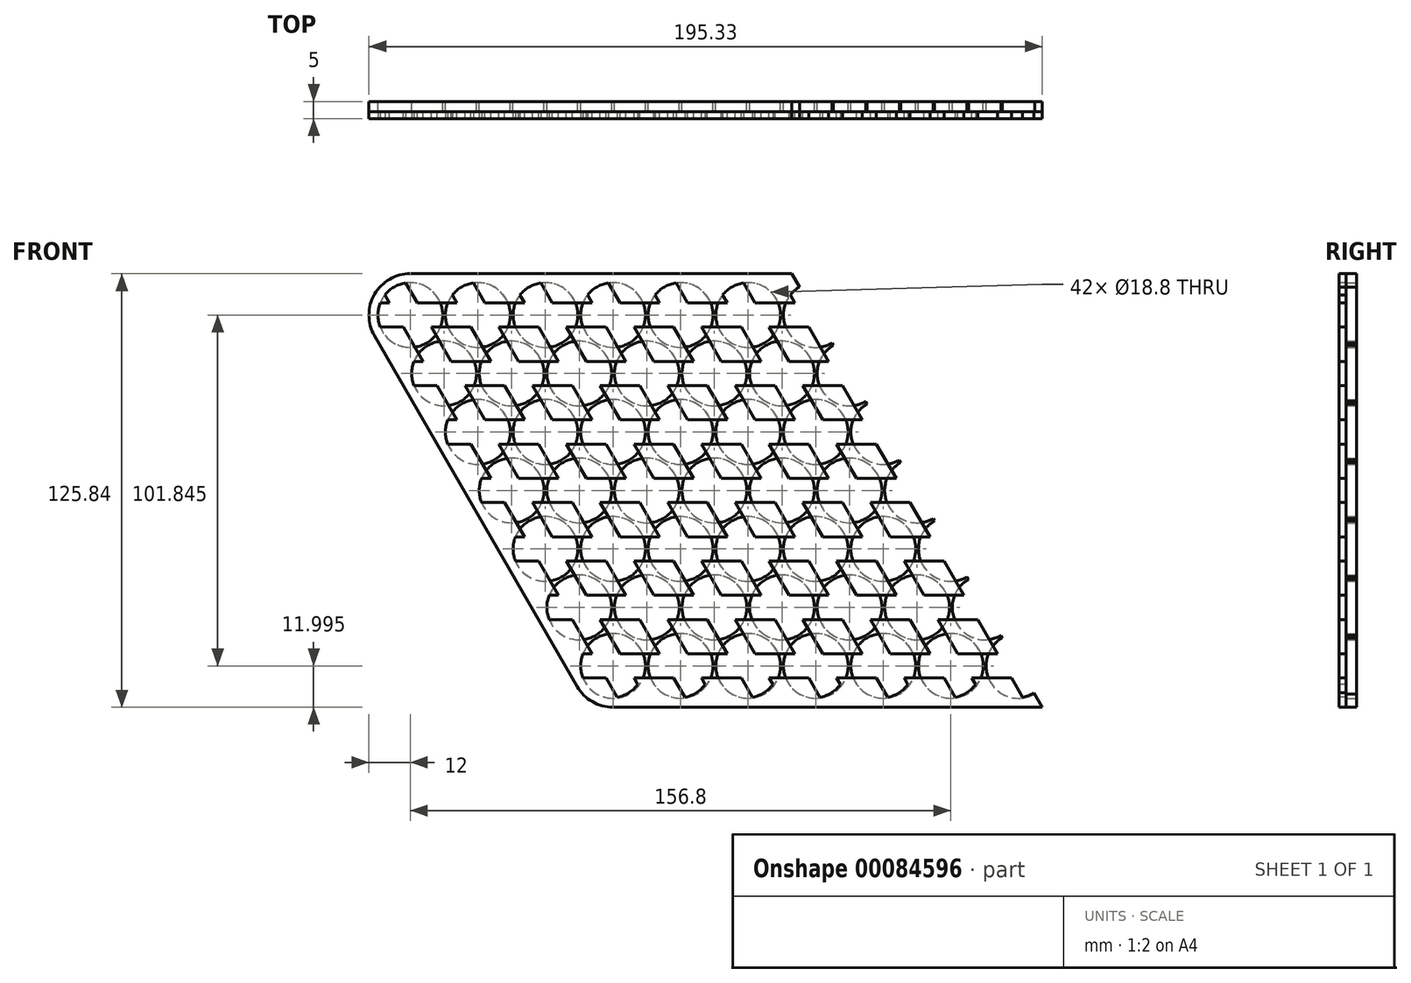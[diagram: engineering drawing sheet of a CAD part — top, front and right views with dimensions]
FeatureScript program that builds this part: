
annotation { "Feature Type Name" : "Feature", "Feature Type Description" : "" }
export const myFeature = defineFeature(function(context is Context, id is Id, definition is map)
    precondition{}
    {
        {
            var Q0;
            Q0=qCreatedBy(makeId("Front.planeOp"),FACE);
            var sketch = newSketch(context, id + "F0", { "sketchPlane" : qUnion([Q0]) });
            skLineSegment(sketch, "E0", {"start": v(0, 0) * mm, "end": v(79.44, 0) * mm, "construction": true});
            skLineSegment(sketch, "E1", {"start": v(0, 0) * mm, "end": v(43.4, -75.16) * mm, "construction": true});
            skCircle(sketch, "E2", {"center": v(0, 0) * mm, "radius": 9.4 * mm});
            skCircle(sketch, "E3.1.0.0", {"center": v(19.6, 0) * mm, "radius": 9.4 * mm});
            skCircle(sketch, "E3.2.0.0", {"center": v(39.2, 0) * mm, "radius": 9.4 * mm});
            skCircle(sketch, "E3.3.0.0", {"center": v(58.8, 0) * mm, "radius": 9.4 * mm});
            skCircle(sketch, "E3.4.0.0", {"center": v(78.4, 0) * mm, "radius": 9.4 * mm});
            skCircle(sketch, "E3.5.0.0", {"center": v(98, 0) * mm, "radius": 9.4 * mm});
            skCircle(sketch, "E3.6.0.0", {"center": v(117.6, 0) * mm, "radius": 9.4 * mm});
            skCircle(sketch, "E3.7.0.0", {"center": v(137.2, 0) * mm, "radius": 9.4 * mm});
            skCircle(sketch, "E3.8.0.0", {"center": v(156.8, 0) * mm, "radius": 9.4 * mm});
            skCircle(sketch, "E3.9.0.0", {"center": v(176.4, 0) * mm, "radius": 9.4 * mm});
            skCircle(sketch, "E3.10.0.0", {"center": v(196, 0) * mm, "radius": 9.4 * mm});
            skCircle(sketch, "E3.11.0.0", {"center": v(215.6, 0) * mm, "radius": 9.4 * mm});
            skCircle(sketch, "E3.12.0.0", {"center": v(235.2, 0) * mm, "radius": 9.4 * mm});
            skCircle(sketch, "E3.13.0.0", {"center": v(254.8, 0) * mm, "radius": 9.4 * mm});
            skCircle(sketch, "E3.14.0.0", {"center": v(274.4, 0) * mm, "radius": 9.4 * mm});
            skCircle(sketch, "E3.15.0.0", {"center": v(294, 0) * mm, "radius": 9.4 * mm});
            skCircle(sketch, "E3.16.0.0", {"center": v(313.6, 0) * mm, "radius": 9.4 * mm});
            skCircle(sketch, "E3.17.0.0", {"center": v(333.2, 0) * mm, "radius": 9.4 * mm});
            skCircle(sketch, "E3.18.0.0", {"center": v(352.8, 0) * mm, "radius": 9.4 * mm});
            skCircle(sketch, "E3.19.0.0", {"center": v(372.4, 0) * mm, "radius": 9.4 * mm});
            skLineSegment(sketch, "E3.direction1", {"start": v(0, 0) * mm, "end": v(19.6, 0) * mm, "construction": true});
            skCircle(sketch, "E4.1.0.0", {"center": v(9.8, -16.97) * mm, "radius": 9.4 * mm});
            skCircle(sketch, "E4.2.0.0", {"center": v(19.6, -33.95) * mm, "radius": 9.4 * mm});
            skCircle(sketch, "E4.3.0.0", {"center": v(29.4, -50.92) * mm, "radius": 9.4 * mm});
            skCircle(sketch, "E4.4.0.0", {"center": v(39.2, -67.9) * mm, "radius": 9.4 * mm});
            skCircle(sketch, "E4.5.0.0", {"center": v(49, -84.87) * mm, "radius": 9.4 * mm});
            skCircle(sketch, "E4.6.0.0", {"center": v(58.8, -101.84) * mm, "radius": 9.4 * mm});
            skLineSegment(sketch, "E4.direction1", {"start": v(0, 0) * mm, "end": v(9.8, -16.97) * mm, "construction": true});
            skCircle(sketch, "E5.1.0.0", {"center": v(29.4, -16.97) * mm, "radius": 9.4 * mm});
            skCircle(sketch, "E5.1.0.1", {"center": v(39.2, -33.95) * mm, "radius": 9.4 * mm});
            skCircle(sketch, "E5.1.0.2", {"center": v(49, -50.92) * mm, "radius": 9.4 * mm});
            skCircle(sketch, "E5.1.0.3", {"center": v(58.8, -67.9) * mm, "radius": 9.4 * mm});
            skCircle(sketch, "E5.1.0.4", {"center": v(68.6, -84.87) * mm, "radius": 9.4 * mm});
            skCircle(sketch, "E5.1.0.5", {"center": v(78.4, -101.84) * mm, "radius": 9.4 * mm});
            skCircle(sketch, "E5.2.0.0", {"center": v(49, -16.97) * mm, "radius": 9.4 * mm});
            skCircle(sketch, "E5.2.0.1", {"center": v(58.8, -33.95) * mm, "radius": 9.4 * mm});
            skCircle(sketch, "E5.2.0.2", {"center": v(68.6, -50.92) * mm, "radius": 9.4 * mm});
            skCircle(sketch, "E5.2.0.3", {"center": v(78.4, -67.9) * mm, "radius": 9.4 * mm});
            skCircle(sketch, "E5.2.0.4", {"center": v(88.2, -84.87) * mm, "radius": 9.4 * mm});
            skCircle(sketch, "E5.2.0.5", {"center": v(98, -101.84) * mm, "radius": 9.4 * mm});
            skCircle(sketch, "E5.3.0.0", {"center": v(68.6, -16.97) * mm, "radius": 9.4 * mm});
            skCircle(sketch, "E5.3.0.1", {"center": v(78.4, -33.95) * mm, "radius": 9.4 * mm});
            skCircle(sketch, "E5.3.0.2", {"center": v(88.2, -50.92) * mm, "radius": 9.4 * mm});
            skCircle(sketch, "E5.3.0.3", {"center": v(98, -67.9) * mm, "radius": 9.4 * mm});
            skCircle(sketch, "E5.3.0.4", {"center": v(107.8, -84.87) * mm, "radius": 9.4 * mm});
            skCircle(sketch, "E5.3.0.5", {"center": v(117.6, -101.84) * mm, "radius": 9.4 * mm});
            skCircle(sketch, "E5.4.0.0", {"center": v(88.2, -16.97) * mm, "radius": 9.4 * mm});
            skCircle(sketch, "E5.4.0.1", {"center": v(98, -33.95) * mm, "radius": 9.4 * mm});
            skCircle(sketch, "E5.4.0.2", {"center": v(107.8, -50.92) * mm, "radius": 9.4 * mm});
            skCircle(sketch, "E5.4.0.3", {"center": v(117.6, -67.9) * mm, "radius": 9.4 * mm});
            skCircle(sketch, "E5.4.0.4", {"center": v(127.4, -84.87) * mm, "radius": 9.4 * mm});
            skCircle(sketch, "E5.4.0.5", {"center": v(137.2, -101.84) * mm, "radius": 9.4 * mm});
            skCircle(sketch, "E5.5.0.0", {"center": v(107.8, -16.97) * mm, "radius": 9.4 * mm});
            skCircle(sketch, "E5.5.0.1", {"center": v(117.6, -33.95) * mm, "radius": 9.4 * mm});
            skCircle(sketch, "E5.5.0.2", {"center": v(127.4, -50.92) * mm, "radius": 9.4 * mm});
            skCircle(sketch, "E5.5.0.3", {"center": v(137.2, -67.9) * mm, "radius": 9.4 * mm});
            skCircle(sketch, "E5.5.0.4", {"center": v(147, -84.87) * mm, "radius": 9.4 * mm});
            skCircle(sketch, "E5.5.0.5", {"center": v(156.8, -101.84) * mm, "radius": 9.4 * mm});
            skCircle(sketch, "E5.6.0.0", {"center": v(127.4, -16.97) * mm, "radius": 9.4 * mm});
            skCircle(sketch, "E5.6.0.1", {"center": v(137.2, -33.95) * mm, "radius": 9.4 * mm});
            skCircle(sketch, "E5.6.0.2", {"center": v(147, -50.92) * mm, "radius": 9.4 * mm});
            skCircle(sketch, "E5.6.0.3", {"center": v(156.8, -67.9) * mm, "radius": 9.4 * mm});
            skCircle(sketch, "E5.6.0.4", {"center": v(166.6, -84.87) * mm, "radius": 9.4 * mm});
            skCircle(sketch, "E5.6.0.5", {"center": v(176.4, -101.84) * mm, "radius": 9.4 * mm});
            skCircle(sketch, "E5.7.0.0", {"center": v(147, -16.97) * mm, "radius": 9.4 * mm});
            skCircle(sketch, "E5.7.0.1", {"center": v(156.8, -33.95) * mm, "radius": 9.4 * mm});
            skCircle(sketch, "E5.7.0.2", {"center": v(166.6, -50.92) * mm, "radius": 9.4 * mm});
            skCircle(sketch, "E5.7.0.3", {"center": v(176.4, -67.9) * mm, "radius": 9.4 * mm});
            skCircle(sketch, "E5.7.0.4", {"center": v(186.2, -84.87) * mm, "radius": 9.4 * mm});
            skCircle(sketch, "E5.7.0.5", {"center": v(196, -101.84) * mm, "radius": 9.4 * mm});
            skCircle(sketch, "E5.8.0.0", {"center": v(166.6, -16.97) * mm, "radius": 9.4 * mm});
            skCircle(sketch, "E5.8.0.1", {"center": v(176.4, -33.95) * mm, "radius": 9.4 * mm});
            skCircle(sketch, "E5.8.0.2", {"center": v(186.2, -50.92) * mm, "radius": 9.4 * mm});
            skCircle(sketch, "E5.8.0.3", {"center": v(196, -67.9) * mm, "radius": 9.4 * mm});
            skCircle(sketch, "E5.8.0.4", {"center": v(205.8, -84.87) * mm, "radius": 9.4 * mm});
            skCircle(sketch, "E5.8.0.5", {"center": v(215.6, -101.84) * mm, "radius": 9.4 * mm});
            skCircle(sketch, "E5.9.0.0", {"center": v(186.2, -16.97) * mm, "radius": 9.4 * mm});
            skCircle(sketch, "E5.9.0.1", {"center": v(196, -33.95) * mm, "radius": 9.4 * mm});
            skCircle(sketch, "E5.9.0.2", {"center": v(205.8, -50.92) * mm, "radius": 9.4 * mm});
            skCircle(sketch, "E5.9.0.3", {"center": v(215.6, -67.9) * mm, "radius": 9.4 * mm});
            skCircle(sketch, "E5.9.0.4", {"center": v(225.4, -84.87) * mm, "radius": 9.4 * mm});
            skCircle(sketch, "E5.9.0.5", {"center": v(235.2, -101.84) * mm, "radius": 9.4 * mm});
            skCircle(sketch, "E5.10.0.0", {"center": v(205.8, -16.97) * mm, "radius": 9.4 * mm});
            skCircle(sketch, "E5.10.0.1", {"center": v(215.6, -33.95) * mm, "radius": 9.4 * mm});
            skCircle(sketch, "E5.10.0.2", {"center": v(225.4, -50.92) * mm, "radius": 9.4 * mm});
            skCircle(sketch, "E5.10.0.3", {"center": v(235.2, -67.9) * mm, "radius": 9.4 * mm});
            skCircle(sketch, "E5.10.0.4", {"center": v(245, -84.87) * mm, "radius": 9.4 * mm});
            skCircle(sketch, "E5.10.0.5", {"center": v(254.8, -101.84) * mm, "radius": 9.4 * mm});
            skCircle(sketch, "E5.11.0.0", {"center": v(225.4, -16.97) * mm, "radius": 9.4 * mm});
            skCircle(sketch, "E5.11.0.1", {"center": v(235.2, -33.95) * mm, "radius": 9.4 * mm});
            skCircle(sketch, "E5.11.0.2", {"center": v(245, -50.92) * mm, "radius": 9.4 * mm});
            skCircle(sketch, "E5.11.0.3", {"center": v(254.8, -67.9) * mm, "radius": 9.4 * mm});
            skCircle(sketch, "E5.11.0.4", {"center": v(264.6, -84.87) * mm, "radius": 9.4 * mm});
            skCircle(sketch, "E5.11.0.5", {"center": v(274.4, -101.84) * mm, "radius": 9.4 * mm});
            skCircle(sketch, "E5.12.0.0", {"center": v(245, -16.97) * mm, "radius": 9.4 * mm});
            skCircle(sketch, "E5.12.0.1", {"center": v(254.8, -33.95) * mm, "radius": 9.4 * mm});
            skCircle(sketch, "E5.12.0.2", {"center": v(264.6, -50.92) * mm, "radius": 9.4 * mm});
            skCircle(sketch, "E5.12.0.3", {"center": v(274.4, -67.9) * mm, "radius": 9.4 * mm});
            skCircle(sketch, "E5.12.0.4", {"center": v(284.2, -84.87) * mm, "radius": 9.4 * mm});
            skCircle(sketch, "E5.12.0.5", {"center": v(294, -101.84) * mm, "radius": 9.4 * mm});
            skCircle(sketch, "E5.13.0.0", {"center": v(264.6, -16.97) * mm, "radius": 9.4 * mm});
            skCircle(sketch, "E5.13.0.1", {"center": v(274.4, -33.95) * mm, "radius": 9.4 * mm});
            skCircle(sketch, "E5.13.0.2", {"center": v(284.2, -50.92) * mm, "radius": 9.4 * mm});
            skCircle(sketch, "E5.13.0.3", {"center": v(294, -67.9) * mm, "radius": 9.4 * mm});
            skCircle(sketch, "E5.13.0.4", {"center": v(303.8, -84.87) * mm, "radius": 9.4 * mm});
            skCircle(sketch, "E5.13.0.5", {"center": v(313.6, -101.84) * mm, "radius": 9.4 * mm});
            skCircle(sketch, "E5.14.0.0", {"center": v(284.2, -16.97) * mm, "radius": 9.4 * mm});
            skCircle(sketch, "E5.14.0.1", {"center": v(294, -33.95) * mm, "radius": 9.4 * mm});
            skCircle(sketch, "E5.14.0.2", {"center": v(303.8, -50.92) * mm, "radius": 9.4 * mm});
            skCircle(sketch, "E5.14.0.3", {"center": v(313.6, -67.9) * mm, "radius": 9.4 * mm});
            skCircle(sketch, "E5.14.0.4", {"center": v(323.4, -84.87) * mm, "radius": 9.4 * mm});
            skCircle(sketch, "E5.14.0.5", {"center": v(333.2, -101.84) * mm, "radius": 9.4 * mm});
            skCircle(sketch, "E5.15.0.0", {"center": v(303.8, -16.97) * mm, "radius": 9.4 * mm});
            skCircle(sketch, "E5.15.0.1", {"center": v(313.6, -33.95) * mm, "radius": 9.4 * mm});
            skCircle(sketch, "E5.15.0.2", {"center": v(323.4, -50.92) * mm, "radius": 9.4 * mm});
            skCircle(sketch, "E5.15.0.3", {"center": v(333.2, -67.9) * mm, "radius": 9.4 * mm});
            skCircle(sketch, "E5.15.0.4", {"center": v(343, -84.87) * mm, "radius": 9.4 * mm});
            skCircle(sketch, "E5.15.0.5", {"center": v(352.8, -101.84) * mm, "radius": 9.4 * mm});
            skCircle(sketch, "E5.16.0.0", {"center": v(323.4, -16.97) * mm, "radius": 9.4 * mm});
            skCircle(sketch, "E5.16.0.1", {"center": v(333.2, -33.95) * mm, "radius": 9.4 * mm});
            skCircle(sketch, "E5.16.0.2", {"center": v(343, -50.92) * mm, "radius": 9.4 * mm});
            skCircle(sketch, "E5.16.0.3", {"center": v(352.8, -67.9) * mm, "radius": 9.4 * mm});
            skCircle(sketch, "E5.16.0.4", {"center": v(362.6, -84.87) * mm, "radius": 9.4 * mm});
            skCircle(sketch, "E5.16.0.5", {"center": v(372.4, -101.84) * mm, "radius": 9.4 * mm});
            skCircle(sketch, "E5.17.0.0", {"center": v(343, -16.97) * mm, "radius": 9.4 * mm});
            skCircle(sketch, "E5.17.0.1", {"center": v(352.8, -33.95) * mm, "radius": 9.4 * mm});
            skCircle(sketch, "E5.17.0.2", {"center": v(362.6, -50.92) * mm, "radius": 9.4 * mm});
            skCircle(sketch, "E5.17.0.3", {"center": v(372.4, -67.9) * mm, "radius": 9.4 * mm});
            skCircle(sketch, "E5.17.0.4", {"center": v(382.2, -84.87) * mm, "radius": 9.4 * mm});
            skCircle(sketch, "E5.17.0.5", {"center": v(392, -101.84) * mm, "radius": 9.4 * mm});
            skCircle(sketch, "E5.18.0.0", {"center": v(362.6, -16.97) * mm, "radius": 9.4 * mm});
            skCircle(sketch, "E5.18.0.1", {"center": v(372.4, -33.95) * mm, "radius": 9.4 * mm});
            skCircle(sketch, "E5.18.0.2", {"center": v(382.2, -50.92) * mm, "radius": 9.4 * mm});
            skCircle(sketch, "E5.18.0.3", {"center": v(392, -67.9) * mm, "radius": 9.4 * mm});
            skCircle(sketch, "E5.18.0.4", {"center": v(401.8, -84.87) * mm, "radius": 9.4 * mm});
            skCircle(sketch, "E5.18.0.5", {"center": v(411.6, -101.84) * mm, "radius": 9.4 * mm});
            skCircle(sketch, "E5.19.0.0", {"center": v(382.2, -16.97) * mm, "radius": 9.4 * mm});
            skCircle(sketch, "E5.19.0.1", {"center": v(392, -33.95) * mm, "radius": 9.4 * mm});
            skCircle(sketch, "E5.19.0.2", {"center": v(401.8, -50.92) * mm, "radius": 9.4 * mm});
            skCircle(sketch, "E5.19.0.3", {"center": v(411.6, -67.9) * mm, "radius": 9.4 * mm});
            skCircle(sketch, "E5.19.0.4", {"center": v(421.4, -84.87) * mm, "radius": 9.4 * mm});
            skCircle(sketch, "E5.19.0.5", {"center": v(431.2, -101.84) * mm, "radius": 9.4 * mm});
            skLineSegment(sketch, "E5.direction1", {"start": v(9.8, -16.97) * mm, "end": v(29.4, -16.97) * mm, "construction": true});
            skLineSegment(sketch, "E6", {"start": v(0, 0) * mm, "end": v(372.4, 0) * mm, "construction": true});
            skLineSegment(sketch, "E7", {"start": v(372.4, 0) * mm, "end": v(441, -118.82) * mm, "construction": true});
            skLineSegment(sketch, "E8", {"start": v(441, -118.82) * mm, "end": v(68.6, -118.82) * mm, "construction": true});
            skLineSegment(sketch, "E9", {"start": v(68.6, -118.82) * mm, "end": v(0, 0) * mm, "construction": true});
            skArc(sketch, "E10", {"start": v(48.4, -107.84) * mm, "mid": v(52.8, -112.24) * mm, "end": v(58.8, -113.84) * mm});
            skArc(sketch, "E11", {"start": v(431.2, -113.84) * mm, "mid": v(441.6, -107.84) * mm, "end": v(441.6, -95.84) * mm});
            skArc(sketch, "E12", {"start": v(382.8, 6) * mm, "mid": v(378.4, 10.4) * mm, "end": v(372.4, 12) * mm});
            skArc(sketch, "E13", {"start": v(0, 12) * mm, "mid": v(-10.4, 6) * mm, "end": v(-10.4, -6) * mm});
            skLineSegment(sketch, "E14", {"start": v(0, 12) * mm, "end": v(372.4, 12) * mm});
            skLineSegment(sketch, "E15", {"start": v(-10.4, -6) * mm, "end": v(48.4, -107.84) * mm});
            skLineSegment(sketch, "E16", {"start": v(58.8, -113.84) * mm, "end": v(431.2, -113.84) * mm});
            skLineSegment(sketch, "E17", {"start": v(441.6, -95.84) * mm, "end": v(382.8, 6) * mm});
            skLineSegment(sketch, "E18", {"start": v(441.6, -107.84) * mm, "end": v(500.4, -6) * mm, "construction": true});
            skLineSegment(sketch, "E19", {"start": v(372.4, 12) * mm, "end": v(490, 12) * mm, "construction": true});
            skPoint(sketch, "E20.visualSharp", {"position": v(510.78, 12) * mm});
            skArc(sketch, "E20.filletArc", {"start": v(500.4, -6) * mm, "mid": v(500.4, 6) * mm, "end": v(490, 12) * mm, "construction": true});
            skSolve(sketch);
        }
        {
            var Q0;
            Q0=makeQuery(id+"F0.imprint","IMPRINT",FACE,{"disambiguationData":[TD([[makeQuery(id+"F0.imprint","IMPRINT",EDGE,{"derivedFrom":sQuery(id+"F0.wireOp",EDGE,"E2")}),-1.0]])]});
            extrude(context, id + "F1", {"entities" : qUnion([Q0]), "depth" : 3 * mm});
        }
        {
            var Q0;
            Q0=makeQuery(id+"F1.opExtrude","CAP_FACE",FACE,{"disambiguationData":[OSD([sQuery(id+"F0.wireOp",EDGE,"E2"),sQuery(id+"F0.wireOp",EDGE,"E3.1.0.0"),sQuery(id+"F0.wireOp",EDGE,"E3.2.0.0"),sQuery(id+"F0.wireOp",EDGE,"E3.3.0.0"),sQuery(id+"F0.wireOp",EDGE,"E3.4.0.0"),sQuery(id+"F0.wireOp",EDGE,"E3.5.0.0"),sQuery(id+"F0.wireOp",EDGE,"E3.6.0.0"),sQuery(id+"F0.wireOp",EDGE,"E3.7.0.0"),sQuery(id+"F0.wireOp",EDGE,"E3.8.0.0"),sQuery(id+"F0.wireOp",EDGE,"E3.9.0.0"),sQuery(id+"F0.wireOp",EDGE,"E3.10.0.0"),sQuery(id+"F0.wireOp",EDGE,"E3.11.0.0"),sQuery(id+"F0.wireOp",EDGE,"E3.12.0.0"),sQuery(id+"F0.wireOp",EDGE,"E3.13.0.0"),sQuery(id+"F0.wireOp",EDGE,"E3.14.0.0"),sQuery(id+"F0.wireOp",EDGE,"E3.15.0.0"),sQuery(id+"F0.wireOp",EDGE,"E3.16.0.0"),sQuery(id+"F0.wireOp",EDGE,"E3.17.0.0"),sQuery(id+"F0.wireOp",EDGE,"E3.18.0.0"),sQuery(id+"F0.wireOp",EDGE,"E3.19.0.0"),sQuery(id+"F0.wireOp",EDGE,"E4.1.0.0"),sQuery(id+"F0.wireOp",EDGE,"E4.2.0.0"),sQuery(id+"F0.wireOp",EDGE,"E4.3.0.0"),sQuery(id+"F0.wireOp",EDGE,"E4.4.0.0"),sQuery(id+"F0.wireOp",EDGE,"E4.5.0.0"),sQuery(id+"F0.wireOp",EDGE,"E4.6.0.0"),sQuery(id+"F0.wireOp",EDGE,"E5.1.0.0"),sQuery(id+"F0.wireOp",EDGE,"E5.1.0.1"),sQuery(id+"F0.wireOp",EDGE,"E5.1.0.2"),sQuery(id+"F0.wireOp",EDGE,"E5.1.0.3"),sQuery(id+"F0.wireOp",EDGE,"E5.1.0.4"),sQuery(id+"F0.wireOp",EDGE,"E5.1.0.5"),sQuery(id+"F0.wireOp",EDGE,"E5.2.0.0"),sQuery(id+"F0.wireOp",EDGE,"E5.2.0.1"),sQuery(id+"F0.wireOp",EDGE,"E5.2.0.2"),sQuery(id+"F0.wireOp",EDGE,"E5.2.0.3"),sQuery(id+"F0.wireOp",EDGE,"E5.2.0.4"),sQuery(id+"F0.wireOp",EDGE,"E5.2.0.5"),sQuery(id+"F0.wireOp",EDGE,"E5.3.0.0"),sQuery(id+"F0.wireOp",EDGE,"E5.3.0.1"),sQuery(id+"F0.wireOp",EDGE,"E5.3.0.2"),sQuery(id+"F0.wireOp",EDGE,"E5.3.0.3"),sQuery(id+"F0.wireOp",EDGE,"E5.3.0.4"),sQuery(id+"F0.wireOp",EDGE,"E5.3.0.5"),sQuery(id+"F0.wireOp",EDGE,"E5.4.0.0"),sQuery(id+"F0.wireOp",EDGE,"E5.4.0.1"),sQuery(id+"F0.wireOp",EDGE,"E5.4.0.2"),sQuery(id+"F0.wireOp",EDGE,"E5.4.0.3"),sQuery(id+"F0.wireOp",EDGE,"E5.4.0.4"),sQuery(id+"F0.wireOp",EDGE,"E5.4.0.5"),sQuery(id+"F0.wireOp",EDGE,"E5.5.0.0"),sQuery(id+"F0.wireOp",EDGE,"E5.5.0.1"),sQuery(id+"F0.wireOp",EDGE,"E5.5.0.2"),sQuery(id+"F0.wireOp",EDGE,"E5.5.0.3"),sQuery(id+"F0.wireOp",EDGE,"E5.5.0.4"),sQuery(id+"F0.wireOp",EDGE,"E5.5.0.5"),sQuery(id+"F0.wireOp",EDGE,"E5.6.0.0"),sQuery(id+"F0.wireOp",EDGE,"E5.6.0.1"),sQuery(id+"F0.wireOp",EDGE,"E5.6.0.2"),sQuery(id+"F0.wireOp",EDGE,"E5.6.0.3"),sQuery(id+"F0.wireOp",EDGE,"E5.6.0.4"),sQuery(id+"F0.wireOp",EDGE,"E5.6.0.5"),sQuery(id+"F0.wireOp",EDGE,"E5.7.0.0"),sQuery(id+"F0.wireOp",EDGE,"E5.7.0.1"),sQuery(id+"F0.wireOp",EDGE,"E5.7.0.2"),sQuery(id+"F0.wireOp",EDGE,"E5.7.0.3"),sQuery(id+"F0.wireOp",EDGE,"E5.7.0.4"),sQuery(id+"F0.wireOp",EDGE,"E5.7.0.5"),sQuery(id+"F0.wireOp",EDGE,"E5.8.0.0"),sQuery(id+"F0.wireOp",EDGE,"E5.8.0.1"),sQuery(id+"F0.wireOp",EDGE,"E5.8.0.2"),sQuery(id+"F0.wireOp",EDGE,"E5.8.0.3"),sQuery(id+"F0.wireOp",EDGE,"E5.8.0.4"),sQuery(id+"F0.wireOp",EDGE,"E5.8.0.5"),sQuery(id+"F0.wireOp",EDGE,"E5.9.0.0"),sQuery(id+"F0.wireOp",EDGE,"E5.9.0.1"),sQuery(id+"F0.wireOp",EDGE,"E5.9.0.2"),sQuery(id+"F0.wireOp",EDGE,"E5.9.0.3"),sQuery(id+"F0.wireOp",EDGE,"E5.9.0.4"),sQuery(id+"F0.wireOp",EDGE,"E5.9.0.5"),sQuery(id+"F0.wireOp",EDGE,"E5.10.0.0"),sQuery(id+"F0.wireOp",EDGE,"E5.10.0.1"),sQuery(id+"F0.wireOp",EDGE,"E5.10.0.2"),sQuery(id+"F0.wireOp",EDGE,"E5.10.0.3"),sQuery(id+"F0.wireOp",EDGE,"E5.10.0.4"),sQuery(id+"F0.wireOp",EDGE,"E5.10.0.5"),sQuery(id+"F0.wireOp",EDGE,"E5.11.0.0"),sQuery(id+"F0.wireOp",EDGE,"E5.11.0.1"),sQuery(id+"F0.wireOp",EDGE,"E5.11.0.2"),sQuery(id+"F0.wireOp",EDGE,"E5.11.0.3"),sQuery(id+"F0.wireOp",EDGE,"E5.11.0.4"),sQuery(id+"F0.wireOp",EDGE,"E5.11.0.5"),sQuery(id+"F0.wireOp",EDGE,"E5.12.0.0"),sQuery(id+"F0.wireOp",EDGE,"E5.12.0.1"),sQuery(id+"F0.wireOp",EDGE,"E5.12.0.2"),sQuery(id+"F0.wireOp",EDGE,"E5.12.0.3"),sQuery(id+"F0.wireOp",EDGE,"E5.12.0.4"),sQuery(id+"F0.wireOp",EDGE,"E5.12.0.5"),sQuery(id+"F0.wireOp",EDGE,"E5.13.0.0"),sQuery(id+"F0.wireOp",EDGE,"E5.13.0.1"),sQuery(id+"F0.wireOp",EDGE,"E5.13.0.2"),sQuery(id+"F0.wireOp",EDGE,"E5.13.0.3"),sQuery(id+"F0.wireOp",EDGE,"E5.13.0.4"),sQuery(id+"F0.wireOp",EDGE,"E5.13.0.5"),sQuery(id+"F0.wireOp",EDGE,"E5.14.0.0"),sQuery(id+"F0.wireOp",EDGE,"E5.14.0.1"),sQuery(id+"F0.wireOp",EDGE,"E5.14.0.2"),sQuery(id+"F0.wireOp",EDGE,"E5.14.0.3"),sQuery(id+"F0.wireOp",EDGE,"E5.14.0.4"),sQuery(id+"F0.wireOp",EDGE,"E5.14.0.5"),sQuery(id+"F0.wireOp",EDGE,"E5.15.0.0"),sQuery(id+"F0.wireOp",EDGE,"E5.15.0.1"),sQuery(id+"F0.wireOp",EDGE,"E5.15.0.2"),sQuery(id+"F0.wireOp",EDGE,"E5.15.0.3"),sQuery(id+"F0.wireOp",EDGE,"E5.15.0.4"),sQuery(id+"F0.wireOp",EDGE,"E5.15.0.5"),sQuery(id+"F0.wireOp",EDGE,"E5.16.0.0"),sQuery(id+"F0.wireOp",EDGE,"E5.16.0.1"),sQuery(id+"F0.wireOp",EDGE,"E5.16.0.2"),sQuery(id+"F0.wireOp",EDGE,"E5.16.0.3"),sQuery(id+"F0.wireOp",EDGE,"E5.16.0.4"),sQuery(id+"F0.wireOp",EDGE,"E5.16.0.5"),sQuery(id+"F0.wireOp",EDGE,"E5.17.0.0"),sQuery(id+"F0.wireOp",EDGE,"E5.17.0.1"),sQuery(id+"F0.wireOp",EDGE,"E5.17.0.2"),sQuery(id+"F0.wireOp",EDGE,"E5.17.0.3"),sQuery(id+"F0.wireOp",EDGE,"E5.17.0.4"),sQuery(id+"F0.wireOp",EDGE,"E5.17.0.5"),sQuery(id+"F0.wireOp",EDGE,"E5.18.0.0"),sQuery(id+"F0.wireOp",EDGE,"E5.18.0.1"),sQuery(id+"F0.wireOp",EDGE,"E5.18.0.2"),sQuery(id+"F0.wireOp",EDGE,"E5.18.0.3"),sQuery(id+"F0.wireOp",EDGE,"E5.18.0.4"),sQuery(id+"F0.wireOp",EDGE,"E5.18.0.5"),sQuery(id+"F0.wireOp",EDGE,"E5.19.0.0"),sQuery(id+"F0.wireOp",EDGE,"E5.19.0.1"),sQuery(id+"F0.wireOp",EDGE,"E5.19.0.2"),sQuery(id+"F0.wireOp",EDGE,"E5.19.0.3"),sQuery(id+"F0.wireOp",EDGE,"E5.19.0.4"),sQuery(id+"F0.wireOp",EDGE,"E5.19.0.5"),sQuery(id+"F0.wireOp",EDGE,"E10"),sQuery(id+"F0.wireOp",EDGE,"E11"),sQuery(id+"F0.wireOp",EDGE,"E12"),sQuery(id+"F0.wireOp",EDGE,"E13"),sQuery(id+"F0.wireOp",EDGE,"E14"),sQuery(id+"F0.wireOp",EDGE,"E15"),sQuery(id+"F0.wireOp",EDGE,"E16"),sQuery(id+"F0.wireOp",EDGE,"E17")])],"isStart":false});
            var sketch = newSketch(context, id + "F2", { "sketchPlane" : qUnion([Q0]) });
            skLineSegment(sketch, "E21.0", {"start": v(0, 12) * mm, "end": v(372.4, 12) * mm});
            skArc(sketch, "E21.1", {"start": v(0, 12) * mm, "mid": v(-10.4, 6) * mm, "end": v(-10.4, -6) * mm});
            skLineSegment(sketch, "E21.2", {"start": v(-10.4, -6) * mm, "end": v(48.4, -107.84) * mm});
            skArc(sketch, "E21.3", {"start": v(382.8, 6) * mm, "mid": v(378.4, 10.4) * mm, "end": v(372.4, 12) * mm});
            skLineSegment(sketch, "E21.4", {"start": v(441.6, -95.84) * mm, "end": v(382.8, 6) * mm});
            skArc(sketch, "E21.5", {"start": v(431.2, -113.84) * mm, "mid": v(441.6, -107.84) * mm, "end": v(441.6, -95.84) * mm});
            skLineSegment(sketch, "E21.6", {"start": v(58.8, -113.84) * mm, "end": v(431.2, -113.84) * mm});
            skArc(sketch, "E21.7", {"start": v(48.4, -107.84) * mm, "mid": v(52.8, -112.24) * mm, "end": v(58.8, -113.84) * mm});
            skSolve(sketch);
        }
        {
            var Q0;
            Q0=qSketchRegion(id+"F2",true);
            extrude(context, id + "F3", {"entities" : qUnion([Q0]), "depth" : 2 * mm});
        }
        {
            var Q0;
            Q0=makeQuery(id+"F3.opExtrude","CAP_FACE",FACE,{"disambiguationData":[OSD([sQuery(id+"F2.wireOp",EDGE,"E21.0"),sQuery(id+"F2.wireOp",EDGE,"E21.1"),sQuery(id+"F2.wireOp",EDGE,"E21.2"),sQuery(id+"F2.wireOp",EDGE,"E21.3"),sQuery(id+"F2.wireOp",EDGE,"E21.4"),sQuery(id+"F2.wireOp",EDGE,"E21.5"),sQuery(id+"F2.wireOp",EDGE,"E21.6"),sQuery(id+"F2.wireOp",EDGE,"E21.7")])],"isStart":false});
            var sketch = newSketch(context, id + "F4", { "sketchPlane" : qUnion([Q0]) });
            skLineSegment(sketch, "E22", {"start": v(0, 0) * mm, "end": v(58.8, -101.84) * mm, "construction": true});
            skLineSegment(sketch, "E23", {"start": v(58.8, -101.84) * mm, "end": v(431.2, -101.84) * mm, "construction": true});
            skLineSegment(sketch, "E24", {"start": v(431.2, -101.84) * mm, "end": v(372.4, 0) * mm, "construction": true});
            skLineSegment(sketch, "E25", {"start": v(372.4, 0) * mm, "end": v(0, 0) * mm, "construction": true});
            skLineSegment(sketch, "E26", {"start": v(-8.72, 3.5) * mm, "end": v(380.69, 3.5) * mm});
            skLineSegment(sketch, "E27.MirrorCS", {"start": v(-8.72, -3.5) * mm, "end": v(380.9, -3.5) * mm});
            skArc(sketch, "E28.0", {"start": v(-8.72, 3.5) * mm, "mid": v(-9.4, 0) * mm, "end": v(-8.72, -3.5) * mm});
            skArc(sketch, "E29.trimOffspring", {"start": v(380.9, -3.5) * mm, "mid": v(381.47, 0.02) * mm, "end": v(380.69, 3.5) * mm});
            skPoint(sketch, "E30.orphan", {"position": v(456.43, 3.5) * mm});
            skPoint(sketch, "E31.orphan", {"position": v(456.43, -3.5) * mm});
            skPoint(sketch, "E32.orphan", {"position": v(-45.25, 3.5) * mm});
            skPoint(sketch, "E33.orphan", {"position": v(-45.25, -3.5) * mm});
            skLineSegment(sketch, "E34.0.1.0", {"start": v(1.08, -13.47) * mm, "end": v(390.49, -13.47) * mm});
            skLineSegment(sketch, "E34.0.1.1", {"start": v(1.08, -20.47) * mm, "end": v(390.7, -20.47) * mm});
            skArc(sketch, "E34.0.1.2", {"start": v(1.08, -13.47) * mm, "mid": v(0.4, -16.97) * mm, "end": v(1.08, -20.47) * mm});
            skArc(sketch, "E34.0.1.3", {"start": v(390.7, -20.47) * mm, "mid": v(391.27, -16.95) * mm, "end": v(390.49, -13.47) * mm});
            skLineSegment(sketch, "E34.0.2.0", {"start": v(10.88, -30.45) * mm, "end": v(400.29, -30.45) * mm});
            skLineSegment(sketch, "E34.0.2.1", {"start": v(10.88, -37.45) * mm, "end": v(400.5, -37.45) * mm});
            skArc(sketch, "E34.0.2.2", {"start": v(10.88, -30.45) * mm, "mid": v(10.2, -33.95) * mm, "end": v(10.88, -37.45) * mm});
            skArc(sketch, "E34.0.2.3", {"start": v(400.5, -37.45) * mm, "mid": v(401.07, -33.93) * mm, "end": v(400.29, -30.45) * mm});
            skLineSegment(sketch, "E34.0.3.0", {"start": v(20.68, -47.42) * mm, "end": v(410.09, -47.42) * mm});
            skLineSegment(sketch, "E34.0.3.1", {"start": v(20.68, -54.42) * mm, "end": v(410.3, -54.42) * mm});
            skArc(sketch, "E34.0.3.2", {"start": v(20.68, -47.42) * mm, "mid": v(20, -50.92) * mm, "end": v(20.68, -54.42) * mm});
            skArc(sketch, "E34.0.3.3", {"start": v(410.3, -54.42) * mm, "mid": v(410.87, -50.9) * mm, "end": v(410.09, -47.42) * mm});
            skLineSegment(sketch, "E34.0.4.0", {"start": v(30.48, -64.4) * mm, "end": v(419.89, -64.4) * mm});
            skLineSegment(sketch, "E34.0.4.1", {"start": v(30.48, -71.4) * mm, "end": v(420.1, -71.4) * mm});
            skArc(sketch, "E34.0.4.2", {"start": v(30.48, -64.4) * mm, "mid": v(29.8, -67.9) * mm, "end": v(30.48, -71.4) * mm});
            skArc(sketch, "E34.0.4.3", {"start": v(420.1, -71.4) * mm, "mid": v(420.67, -67.88) * mm, "end": v(419.89, -64.4) * mm});
            skLineSegment(sketch, "E34.0.5.0", {"start": v(40.28, -81.37) * mm, "end": v(429.69, -81.37) * mm});
            skLineSegment(sketch, "E34.0.5.1", {"start": v(40.28, -88.37) * mm, "end": v(429.9, -88.37) * mm});
            skArc(sketch, "E34.0.5.2", {"start": v(40.28, -81.37) * mm, "mid": v(39.6, -84.87) * mm, "end": v(40.28, -88.37) * mm});
            skArc(sketch, "E34.0.5.3", {"start": v(429.9, -88.37) * mm, "mid": v(430.47, -84.85) * mm, "end": v(429.69, -81.37) * mm});
            skLineSegment(sketch, "E34.0.6.0", {"start": v(50.08, -98.34) * mm, "end": v(439.49, -98.34) * mm});
            skLineSegment(sketch, "E34.0.6.1", {"start": v(50.08, -105.34) * mm, "end": v(439.7, -105.34) * mm});
            skArc(sketch, "E34.0.6.2", {"start": v(50.08, -98.34) * mm, "mid": v(49.4, -101.84) * mm, "end": v(50.08, -105.34) * mm});
            skArc(sketch, "E34.0.6.3", {"start": v(439.7, -105.34) * mm, "mid": v(440.27, -101.82) * mm, "end": v(439.49, -98.34) * mm});
            skLineSegment(sketch, "E34.direction1", {"start": v(-8.72, 3.5) * mm, "end": v(16.28, 3.5) * mm, "construction": true});
            skLineSegment(sketch, "E34.direction2", {"start": v(-8.72, 3.5) * mm, "end": v(1.08, -13.47) * mm, "construction": true});
            skSolve(sketch);
        }
        {
            var Q0;
            Q0=qSketchRegion(id+"F4",true);
            extrude(context, id + "F5", {"entities" : qUnion([Q0]), "operationType" : NewBodyOperationType.REMOVE, "endBound" : BoundingType.UP_TO_NEXT, "oppositeDirection" : true, "depth" : 25 * mm});
        }
        {
            var Q0;
            Q0=makeQuery(id+"F3.opExtrude","CAP_FACE",FACE,{"disambiguationData":[OSD([sQuery(id+"F2.wireOp",EDGE,"E21.0"),sQuery(id+"F2.wireOp",EDGE,"E21.1"),sQuery(id+"F2.wireOp",EDGE,"E21.2"),sQuery(id+"F2.wireOp",EDGE,"E21.3"),sQuery(id+"F2.wireOp",EDGE,"E21.4"),sQuery(id+"F2.wireOp",EDGE,"E21.5"),sQuery(id+"F2.wireOp",EDGE,"E21.6"),sQuery(id+"F2.wireOp",EDGE,"E21.7")])],"isStart":false});
            var sketch = newSketch(context, id + "F6", { "sketchPlane" : qUnion([Q0]) });
            skLineSegment(sketch, "E35", {"start": v(0, 0) * mm, "end": v(58.8, -101.84) * mm, "construction": true});
            skLineSegment(sketch, "E36", {"start": v(-1.33, 9.3) * mm, "end": v(65.94, -107.21) * mm});
            skLineSegment(sketch, "E37.MirrorCS", {"start": v(-7.4, 5.8) * mm, "end": v(60.02, -110.96) * mm});
            skArc(sketch, "E38.0", {"start": v(-1.33, 9.3) * mm, "mid": v(-4.7, 8.14) * mm, "end": v(-7.4, 5.8) * mm});
            skArc(sketch, "E39.trimOffspring", {"start": v(60.02, -110.96) * mm, "mid": v(63.34, -109.66) * mm, "end": v(65.94, -107.21) * mm});
            skPoint(sketch, "E40.orphan", {"position": v(72.39, -132.38) * mm});
            skPoint(sketch, "E41.orphan", {"position": v(78.45, -128.88) * mm});
            skPoint(sketch, "E42.orphan", {"position": v(-7.3, 19.64) * mm});
            skPoint(sketch, "E43.orphan", {"position": v(-13.36, 16.14) * mm});
            skArc(sketch, "E44.1.0.0", {"start": v(18.27, 9.3) * mm, "mid": v(14.9, 8.14) * mm, "end": v(12.2, 5.8) * mm});
            skLineSegment(sketch, "E44.1.0.1", {"start": v(12.2, 5.8) * mm, "end": v(79.62, -110.96) * mm});
            skLineSegment(sketch, "E44.1.0.2", {"start": v(18.27, 9.3) * mm, "end": v(85.54, -107.21) * mm});
            skArc(sketch, "E44.1.0.3", {"start": v(79.62, -110.96) * mm, "mid": v(82.94, -109.66) * mm, "end": v(85.54, -107.21) * mm});
            skArc(sketch, "E44.2.0.0", {"start": v(37.87, 9.3) * mm, "mid": v(34.5, 8.14) * mm, "end": v(31.8, 5.8) * mm});
            skLineSegment(sketch, "E44.2.0.1", {"start": v(31.8, 5.8) * mm, "end": v(99.22, -110.96) * mm});
            skLineSegment(sketch, "E44.2.0.2", {"start": v(37.87, 9.3) * mm, "end": v(105.14, -107.21) * mm});
            skArc(sketch, "E44.2.0.3", {"start": v(99.22, -110.96) * mm, "mid": v(102.54, -109.66) * mm, "end": v(105.14, -107.21) * mm});
            skArc(sketch, "E44.3.0.0", {"start": v(57.47, 9.3) * mm, "mid": v(54.1, 8.14) * mm, "end": v(51.4, 5.8) * mm});
            skLineSegment(sketch, "E44.3.0.1", {"start": v(51.4, 5.8) * mm, "end": v(118.82, -110.96) * mm});
            skLineSegment(sketch, "E44.3.0.2", {"start": v(57.47, 9.3) * mm, "end": v(124.74, -107.21) * mm});
            skArc(sketch, "E44.3.0.3", {"start": v(118.82, -110.96) * mm, "mid": v(122.14, -109.66) * mm, "end": v(124.74, -107.21) * mm});
            skArc(sketch, "E44.4.0.0", {"start": v(77.07, 9.3) * mm, "mid": v(73.7, 8.14) * mm, "end": v(71, 5.8) * mm});
            skLineSegment(sketch, "E44.4.0.1", {"start": v(71, 5.8) * mm, "end": v(138.42, -110.96) * mm});
            skLineSegment(sketch, "E44.4.0.2", {"start": v(77.07, 9.3) * mm, "end": v(144.34, -107.21) * mm});
            skArc(sketch, "E44.4.0.3", {"start": v(138.42, -110.96) * mm, "mid": v(141.74, -109.66) * mm, "end": v(144.34, -107.21) * mm});
            skArc(sketch, "E44.5.0.0", {"start": v(96.67, 9.3) * mm, "mid": v(93.3, 8.14) * mm, "end": v(90.6, 5.8) * mm});
            skLineSegment(sketch, "E44.5.0.1", {"start": v(90.6, 5.8) * mm, "end": v(158.02, -110.96) * mm});
            skLineSegment(sketch, "E44.5.0.2", {"start": v(96.67, 9.3) * mm, "end": v(163.94, -107.21) * mm});
            skArc(sketch, "E44.5.0.3", {"start": v(158.02, -110.96) * mm, "mid": v(161.34, -109.66) * mm, "end": v(163.94, -107.21) * mm});
            skArc(sketch, "E44.6.0.0", {"start": v(116.27, 9.3) * mm, "mid": v(112.9, 8.14) * mm, "end": v(110.2, 5.8) * mm});
            skLineSegment(sketch, "E44.6.0.1", {"start": v(110.2, 5.8) * mm, "end": v(177.62, -110.96) * mm});
            skLineSegment(sketch, "E44.6.0.2", {"start": v(116.27, 9.3) * mm, "end": v(183.54, -107.21) * mm});
            skArc(sketch, "E44.6.0.3", {"start": v(177.62, -110.96) * mm, "mid": v(180.94, -109.66) * mm, "end": v(183.54, -107.21) * mm});
            skArc(sketch, "E44.7.0.0", {"start": v(135.87, 9.3) * mm, "mid": v(132.5, 8.14) * mm, "end": v(129.8, 5.8) * mm});
            skLineSegment(sketch, "E44.7.0.1", {"start": v(129.8, 5.8) * mm, "end": v(197.22, -110.96) * mm});
            skLineSegment(sketch, "E44.7.0.2", {"start": v(135.87, 9.3) * mm, "end": v(203.14, -107.21) * mm});
            skArc(sketch, "E44.7.0.3", {"start": v(197.22, -110.96) * mm, "mid": v(200.54, -109.66) * mm, "end": v(203.14, -107.21) * mm});
            skArc(sketch, "E44.8.0.0", {"start": v(155.47, 9.3) * mm, "mid": v(152.1, 8.14) * mm, "end": v(149.4, 5.8) * mm});
            skLineSegment(sketch, "E44.8.0.1", {"start": v(149.4, 5.8) * mm, "end": v(216.82, -110.96) * mm});
            skLineSegment(sketch, "E44.8.0.2", {"start": v(155.47, 9.3) * mm, "end": v(222.74, -107.21) * mm});
            skArc(sketch, "E44.8.0.3", {"start": v(216.82, -110.96) * mm, "mid": v(220.14, -109.66) * mm, "end": v(222.74, -107.21) * mm});
            skArc(sketch, "E44.9.0.0", {"start": v(175.07, 9.3) * mm, "mid": v(171.7, 8.14) * mm, "end": v(169, 5.8) * mm});
            skLineSegment(sketch, "E44.9.0.1", {"start": v(169, 5.8) * mm, "end": v(236.42, -110.96) * mm});
            skLineSegment(sketch, "E44.9.0.2", {"start": v(175.07, 9.3) * mm, "end": v(242.34, -107.21) * mm});
            skArc(sketch, "E44.9.0.3", {"start": v(236.42, -110.96) * mm, "mid": v(239.74, -109.66) * mm, "end": v(242.34, -107.21) * mm});
            skArc(sketch, "E44.10.0.0", {"start": v(194.67, 9.3) * mm, "mid": v(191.3, 8.14) * mm, "end": v(188.6, 5.8) * mm});
            skLineSegment(sketch, "E44.10.0.1", {"start": v(188.6, 5.8) * mm, "end": v(256.02, -110.96) * mm});
            skLineSegment(sketch, "E44.10.0.2", {"start": v(194.67, 9.3) * mm, "end": v(261.94, -107.21) * mm});
            skArc(sketch, "E44.10.0.3", {"start": v(256.02, -110.96) * mm, "mid": v(259.34, -109.66) * mm, "end": v(261.94, -107.21) * mm});
            skArc(sketch, "E44.11.0.0", {"start": v(214.27, 9.3) * mm, "mid": v(210.9, 8.14) * mm, "end": v(208.2, 5.8) * mm});
            skLineSegment(sketch, "E44.11.0.1", {"start": v(208.2, 5.8) * mm, "end": v(275.62, -110.96) * mm});
            skLineSegment(sketch, "E44.11.0.2", {"start": v(214.27, 9.3) * mm, "end": v(281.54, -107.21) * mm});
            skArc(sketch, "E44.11.0.3", {"start": v(275.62, -110.96) * mm, "mid": v(278.94, -109.66) * mm, "end": v(281.54, -107.21) * mm});
            skArc(sketch, "E44.12.0.0", {"start": v(233.87, 9.3) * mm, "mid": v(230.5, 8.14) * mm, "end": v(227.8, 5.8) * mm});
            skLineSegment(sketch, "E44.12.0.1", {"start": v(227.8, 5.8) * mm, "end": v(295.22, -110.96) * mm});
            skLineSegment(sketch, "E44.12.0.2", {"start": v(233.87, 9.3) * mm, "end": v(301.14, -107.21) * mm});
            skArc(sketch, "E44.12.0.3", {"start": v(295.22, -110.96) * mm, "mid": v(298.54, -109.66) * mm, "end": v(301.14, -107.21) * mm});
            skArc(sketch, "E44.13.0.0", {"start": v(253.47, 9.3) * mm, "mid": v(250.1, 8.14) * mm, "end": v(247.4, 5.8) * mm});
            skLineSegment(sketch, "E44.13.0.1", {"start": v(247.4, 5.8) * mm, "end": v(314.82, -110.96) * mm});
            skLineSegment(sketch, "E44.13.0.2", {"start": v(253.47, 9.3) * mm, "end": v(320.74, -107.21) * mm});
            skArc(sketch, "E44.13.0.3", {"start": v(314.82, -110.96) * mm, "mid": v(318.14, -109.66) * mm, "end": v(320.74, -107.21) * mm});
            skArc(sketch, "E44.14.0.0", {"start": v(273.07, 9.3) * mm, "mid": v(269.7, 8.14) * mm, "end": v(267, 5.8) * mm});
            skLineSegment(sketch, "E44.14.0.1", {"start": v(267, 5.8) * mm, "end": v(334.42, -110.96) * mm});
            skLineSegment(sketch, "E44.14.0.2", {"start": v(273.07, 9.3) * mm, "end": v(340.34, -107.21) * mm});
            skArc(sketch, "E44.14.0.3", {"start": v(334.42, -110.96) * mm, "mid": v(337.74, -109.66) * mm, "end": v(340.34, -107.21) * mm});
            skArc(sketch, "E44.15.0.0", {"start": v(292.67, 9.3) * mm, "mid": v(289.3, 8.14) * mm, "end": v(286.6, 5.8) * mm});
            skLineSegment(sketch, "E44.15.0.1", {"start": v(286.6, 5.8) * mm, "end": v(354.02, -110.96) * mm});
            skLineSegment(sketch, "E44.15.0.2", {"start": v(292.67, 9.3) * mm, "end": v(359.94, -107.21) * mm});
            skArc(sketch, "E44.15.0.3", {"start": v(354.02, -110.96) * mm, "mid": v(357.34, -109.66) * mm, "end": v(359.94, -107.21) * mm});
            skArc(sketch, "E44.16.0.0", {"start": v(312.27, 9.3) * mm, "mid": v(308.9, 8.14) * mm, "end": v(306.2, 5.8) * mm});
            skLineSegment(sketch, "E44.16.0.1", {"start": v(306.2, 5.8) * mm, "end": v(373.62, -110.96) * mm});
            skLineSegment(sketch, "E44.16.0.2", {"start": v(312.27, 9.3) * mm, "end": v(379.54, -107.21) * mm});
            skArc(sketch, "E44.16.0.3", {"start": v(373.62, -110.96) * mm, "mid": v(376.94, -109.66) * mm, "end": v(379.54, -107.21) * mm});
            skArc(sketch, "E44.17.0.0", {"start": v(331.87, 9.3) * mm, "mid": v(328.5, 8.14) * mm, "end": v(325.8, 5.8) * mm});
            skLineSegment(sketch, "E44.17.0.1", {"start": v(325.8, 5.8) * mm, "end": v(393.22, -110.96) * mm});
            skLineSegment(sketch, "E44.17.0.2", {"start": v(331.87, 9.3) * mm, "end": v(399.14, -107.21) * mm});
            skArc(sketch, "E44.17.0.3", {"start": v(393.22, -110.96) * mm, "mid": v(396.54, -109.66) * mm, "end": v(399.14, -107.21) * mm});
            skArc(sketch, "E44.18.0.0", {"start": v(351.47, 9.3) * mm, "mid": v(348.1, 8.14) * mm, "end": v(345.4, 5.8) * mm});
            skLineSegment(sketch, "E44.18.0.1", {"start": v(345.4, 5.8) * mm, "end": v(412.82, -110.96) * mm});
            skLineSegment(sketch, "E44.18.0.2", {"start": v(351.47, 9.3) * mm, "end": v(418.74, -107.21) * mm});
            skArc(sketch, "E44.18.0.3", {"start": v(412.82, -110.96) * mm, "mid": v(416.14, -109.66) * mm, "end": v(418.74, -107.21) * mm});
            skArc(sketch, "E44.19.0.0", {"start": v(371.07, 9.3) * mm, "mid": v(367.7, 8.14) * mm, "end": v(365, 5.8) * mm});
            skLineSegment(sketch, "E44.19.0.1", {"start": v(365, 5.8) * mm, "end": v(432.42, -110.96) * mm});
            skLineSegment(sketch, "E44.19.0.2", {"start": v(371.07, 9.3) * mm, "end": v(438.34, -107.21) * mm});
            skArc(sketch, "E44.19.0.3", {"start": v(432.42, -110.96) * mm, "mid": v(435.74, -109.66) * mm, "end": v(438.34, -107.21) * mm});
            skLineSegment(sketch, "E44.direction1", {"start": v(-7.4, 5.8) * mm, "end": v(12.2, 5.8) * mm, "construction": true});
            skSolve(sketch);
        }
        {
            var Q0;
            Q0=qSketchRegion(id+"F6",true);
            extrude(context, id + "F7", {"entities" : qUnion([Q0]), "operationType" : NewBodyOperationType.REMOVE, "oppositeDirection" : true, "depth" : 2 * mm});
        }
        {
            var Q0;
            Q0=makeQuery(id+"F1.opExtrude","CAP_FACE",FACE,{"disambiguationData":[OSD([sQuery(id+"F0.wireOp",EDGE,"E2"),sQuery(id+"F0.wireOp",EDGE,"E3.1.0.0"),sQuery(id+"F0.wireOp",EDGE,"E3.2.0.0"),sQuery(id+"F0.wireOp",EDGE,"E3.3.0.0"),sQuery(id+"F0.wireOp",EDGE,"E3.4.0.0"),sQuery(id+"F0.wireOp",EDGE,"E3.5.0.0"),sQuery(id+"F0.wireOp",EDGE,"E3.6.0.0"),sQuery(id+"F0.wireOp",EDGE,"E3.7.0.0"),sQuery(id+"F0.wireOp",EDGE,"E3.8.0.0"),sQuery(id+"F0.wireOp",EDGE,"E3.9.0.0"),sQuery(id+"F0.wireOp",EDGE,"E3.10.0.0"),sQuery(id+"F0.wireOp",EDGE,"E3.11.0.0"),sQuery(id+"F0.wireOp",EDGE,"E3.12.0.0"),sQuery(id+"F0.wireOp",EDGE,"E3.13.0.0"),sQuery(id+"F0.wireOp",EDGE,"E3.14.0.0"),sQuery(id+"F0.wireOp",EDGE,"E3.15.0.0"),sQuery(id+"F0.wireOp",EDGE,"E3.16.0.0"),sQuery(id+"F0.wireOp",EDGE,"E3.17.0.0"),sQuery(id+"F0.wireOp",EDGE,"E3.18.0.0"),sQuery(id+"F0.wireOp",EDGE,"E3.19.0.0"),sQuery(id+"F0.wireOp",EDGE,"E4.1.0.0"),sQuery(id+"F0.wireOp",EDGE,"E4.2.0.0"),sQuery(id+"F0.wireOp",EDGE,"E4.3.0.0"),sQuery(id+"F0.wireOp",EDGE,"E4.4.0.0"),sQuery(id+"F0.wireOp",EDGE,"E4.5.0.0"),sQuery(id+"F0.wireOp",EDGE,"E4.6.0.0"),sQuery(id+"F0.wireOp",EDGE,"E5.1.0.0"),sQuery(id+"F0.wireOp",EDGE,"E5.1.0.1"),sQuery(id+"F0.wireOp",EDGE,"E5.1.0.2"),sQuery(id+"F0.wireOp",EDGE,"E5.1.0.3"),sQuery(id+"F0.wireOp",EDGE,"E5.1.0.4"),sQuery(id+"F0.wireOp",EDGE,"E5.1.0.5"),sQuery(id+"F0.wireOp",EDGE,"E5.2.0.0"),sQuery(id+"F0.wireOp",EDGE,"E5.2.0.1"),sQuery(id+"F0.wireOp",EDGE,"E5.2.0.2"),sQuery(id+"F0.wireOp",EDGE,"E5.2.0.3"),sQuery(id+"F0.wireOp",EDGE,"E5.2.0.4"),sQuery(id+"F0.wireOp",EDGE,"E5.2.0.5"),sQuery(id+"F0.wireOp",EDGE,"E5.3.0.0"),sQuery(id+"F0.wireOp",EDGE,"E5.3.0.1"),sQuery(id+"F0.wireOp",EDGE,"E5.3.0.2"),sQuery(id+"F0.wireOp",EDGE,"E5.3.0.3"),sQuery(id+"F0.wireOp",EDGE,"E5.3.0.4"),sQuery(id+"F0.wireOp",EDGE,"E5.3.0.5"),sQuery(id+"F0.wireOp",EDGE,"E5.4.0.0"),sQuery(id+"F0.wireOp",EDGE,"E5.4.0.1"),sQuery(id+"F0.wireOp",EDGE,"E5.4.0.2"),sQuery(id+"F0.wireOp",EDGE,"E5.4.0.3"),sQuery(id+"F0.wireOp",EDGE,"E5.4.0.4"),sQuery(id+"F0.wireOp",EDGE,"E5.4.0.5"),sQuery(id+"F0.wireOp",EDGE,"E5.5.0.0"),sQuery(id+"F0.wireOp",EDGE,"E5.5.0.1"),sQuery(id+"F0.wireOp",EDGE,"E5.5.0.2"),sQuery(id+"F0.wireOp",EDGE,"E5.5.0.3"),sQuery(id+"F0.wireOp",EDGE,"E5.5.0.4"),sQuery(id+"F0.wireOp",EDGE,"E5.5.0.5"),sQuery(id+"F0.wireOp",EDGE,"E5.6.0.0"),sQuery(id+"F0.wireOp",EDGE,"E5.6.0.1"),sQuery(id+"F0.wireOp",EDGE,"E5.6.0.2"),sQuery(id+"F0.wireOp",EDGE,"E5.6.0.3"),sQuery(id+"F0.wireOp",EDGE,"E5.6.0.4"),sQuery(id+"F0.wireOp",EDGE,"E5.6.0.5"),sQuery(id+"F0.wireOp",EDGE,"E5.7.0.0"),sQuery(id+"F0.wireOp",EDGE,"E5.7.0.1"),sQuery(id+"F0.wireOp",EDGE,"E5.7.0.2"),sQuery(id+"F0.wireOp",EDGE,"E5.7.0.3"),sQuery(id+"F0.wireOp",EDGE,"E5.7.0.4"),sQuery(id+"F0.wireOp",EDGE,"E5.7.0.5"),sQuery(id+"F0.wireOp",EDGE,"E5.8.0.0"),sQuery(id+"F0.wireOp",EDGE,"E5.8.0.1"),sQuery(id+"F0.wireOp",EDGE,"E5.8.0.2"),sQuery(id+"F0.wireOp",EDGE,"E5.8.0.3"),sQuery(id+"F0.wireOp",EDGE,"E5.8.0.4"),sQuery(id+"F0.wireOp",EDGE,"E5.8.0.5"),sQuery(id+"F0.wireOp",EDGE,"E5.9.0.0"),sQuery(id+"F0.wireOp",EDGE,"E5.9.0.1"),sQuery(id+"F0.wireOp",EDGE,"E5.9.0.2"),sQuery(id+"F0.wireOp",EDGE,"E5.9.0.3"),sQuery(id+"F0.wireOp",EDGE,"E5.9.0.4"),sQuery(id+"F0.wireOp",EDGE,"E5.9.0.5"),sQuery(id+"F0.wireOp",EDGE,"E5.10.0.0"),sQuery(id+"F0.wireOp",EDGE,"E5.10.0.1"),sQuery(id+"F0.wireOp",EDGE,"E5.10.0.2"),sQuery(id+"F0.wireOp",EDGE,"E5.10.0.3"),sQuery(id+"F0.wireOp",EDGE,"E5.10.0.4"),sQuery(id+"F0.wireOp",EDGE,"E5.10.0.5"),sQuery(id+"F0.wireOp",EDGE,"E5.11.0.0"),sQuery(id+"F0.wireOp",EDGE,"E5.11.0.1"),sQuery(id+"F0.wireOp",EDGE,"E5.11.0.2"),sQuery(id+"F0.wireOp",EDGE,"E5.11.0.3"),sQuery(id+"F0.wireOp",EDGE,"E5.11.0.4"),sQuery(id+"F0.wireOp",EDGE,"E5.11.0.5"),sQuery(id+"F0.wireOp",EDGE,"E5.12.0.0"),sQuery(id+"F0.wireOp",EDGE,"E5.12.0.1"),sQuery(id+"F0.wireOp",EDGE,"E5.12.0.2"),sQuery(id+"F0.wireOp",EDGE,"E5.12.0.3"),sQuery(id+"F0.wireOp",EDGE,"E5.12.0.4"),sQuery(id+"F0.wireOp",EDGE,"E5.12.0.5"),sQuery(id+"F0.wireOp",EDGE,"E5.13.0.0"),sQuery(id+"F0.wireOp",EDGE,"E5.13.0.1"),sQuery(id+"F0.wireOp",EDGE,"E5.13.0.2"),sQuery(id+"F0.wireOp",EDGE,"E5.13.0.3"),sQuery(id+"F0.wireOp",EDGE,"E5.13.0.4"),sQuery(id+"F0.wireOp",EDGE,"E5.13.0.5"),sQuery(id+"F0.wireOp",EDGE,"E5.14.0.0"),sQuery(id+"F0.wireOp",EDGE,"E5.14.0.1"),sQuery(id+"F0.wireOp",EDGE,"E5.14.0.2"),sQuery(id+"F0.wireOp",EDGE,"E5.14.0.3"),sQuery(id+"F0.wireOp",EDGE,"E5.14.0.4"),sQuery(id+"F0.wireOp",EDGE,"E5.14.0.5"),sQuery(id+"F0.wireOp",EDGE,"E5.15.0.0"),sQuery(id+"F0.wireOp",EDGE,"E5.15.0.1"),sQuery(id+"F0.wireOp",EDGE,"E5.15.0.2"),sQuery(id+"F0.wireOp",EDGE,"E5.15.0.3"),sQuery(id+"F0.wireOp",EDGE,"E5.15.0.4"),sQuery(id+"F0.wireOp",EDGE,"E5.15.0.5"),sQuery(id+"F0.wireOp",EDGE,"E5.16.0.0"),sQuery(id+"F0.wireOp",EDGE,"E5.16.0.1"),sQuery(id+"F0.wireOp",EDGE,"E5.16.0.2"),sQuery(id+"F0.wireOp",EDGE,"E5.16.0.3"),sQuery(id+"F0.wireOp",EDGE,"E5.16.0.4"),sQuery(id+"F0.wireOp",EDGE,"E5.16.0.5"),sQuery(id+"F0.wireOp",EDGE,"E5.17.0.0"),sQuery(id+"F0.wireOp",EDGE,"E5.17.0.1"),sQuery(id+"F0.wireOp",EDGE,"E5.17.0.2"),sQuery(id+"F0.wireOp",EDGE,"E5.17.0.3"),sQuery(id+"F0.wireOp",EDGE,"E5.17.0.4"),sQuery(id+"F0.wireOp",EDGE,"E5.17.0.5"),sQuery(id+"F0.wireOp",EDGE,"E5.18.0.0"),sQuery(id+"F0.wireOp",EDGE,"E5.18.0.1"),sQuery(id+"F0.wireOp",EDGE,"E5.18.0.2"),sQuery(id+"F0.wireOp",EDGE,"E5.18.0.3"),sQuery(id+"F0.wireOp",EDGE,"E5.18.0.4"),sQuery(id+"F0.wireOp",EDGE,"E5.18.0.5"),sQuery(id+"F0.wireOp",EDGE,"E5.19.0.0"),sQuery(id+"F0.wireOp",EDGE,"E5.19.0.1"),sQuery(id+"F0.wireOp",EDGE,"E5.19.0.2"),sQuery(id+"F0.wireOp",EDGE,"E5.19.0.3"),sQuery(id+"F0.wireOp",EDGE,"E5.19.0.4"),sQuery(id+"F0.wireOp",EDGE,"E5.19.0.5"),sQuery(id+"F0.wireOp",EDGE,"E10"),sQuery(id+"F0.wireOp",EDGE,"E11"),sQuery(id+"F0.wireOp",EDGE,"E12"),sQuery(id+"F0.wireOp",EDGE,"E13"),sQuery(id+"F0.wireOp",EDGE,"E14"),sQuery(id+"F0.wireOp",EDGE,"E15"),sQuery(id+"F0.wireOp",EDGE,"E16"),sQuery(id+"F0.wireOp",EDGE,"E17")])],"isStart":true});
            var sketch = newSketch(context, id + "F8", { "sketchPlane" : qUnion([Q0]) });
            skCircle(sketch, "E45.0", {"center": v(-176.4, -101.84) * mm, "radius": 9.4 * mm, "construction": true});
            skCircle(sketch, "E45.1", {"center": v(-117.6, 0) * mm, "radius": 9.4 * mm, "construction": true});
            skLineSegment(sketch, "E46", {"start": v(-117.6, 0) * mm, "end": v(-176.4, -101.84) * mm});
            skLineSegment(sketch, "E47", {"start": v(-176.4, -101.84) * mm, "end": v(-188.39, -122.6) * mm});
            skLineSegment(sketch, "E48", {"start": v(-117.6, 0) * mm, "end": v(-104.72, 22.3) * mm});
            skLineSegment(sketch, "E49", {"start": v(-188.39, -122.6) * mm, "end": v(-476.05, -122.6) * mm});
            skLineSegment(sketch, "E50", {"start": v(-104.72, 22.3) * mm, "end": v(-476.05, 22.3) * mm});
            skLineSegment(sketch, "E51", {"start": v(-476.05, 22.3) * mm, "end": v(-476.05, -122.6) * mm});
            skSolve(sketch);
        }
        {
            var Q0;
            Q0 = qSketchRegion(id + "F8", true);
            extrude(context, id + "F9", {"entities" : qUnion([Q0]), "operationType" : NewBodyOperationType.REMOVE, "endBound" : BoundingType.THROUGH_ALL, "oppositeDirection" : true, "depth" : 25 * mm});
        }
    });
